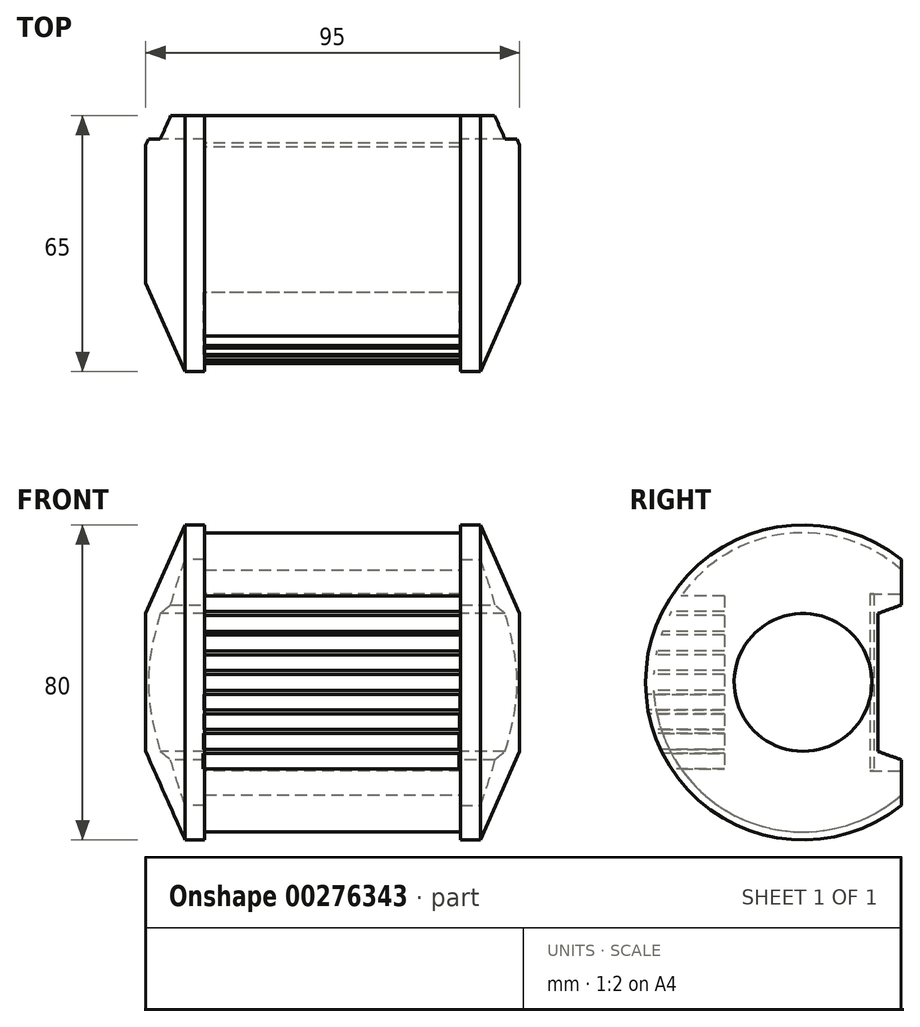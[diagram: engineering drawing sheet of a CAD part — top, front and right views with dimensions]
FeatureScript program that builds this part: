
annotation { "Feature Type Name" : "Feature", "Feature Type Description" : "" }
export const myFeature = defineFeature(function(context is Context, id is Id, definition is map)
    precondition{}
    {
        {
            var Q0;
            Q0=qCreatedBy(makeId("Right.planeOp"),FACE);
            var sketch = newSketch(context, id + "F0", { "sketchPlane" : qUnion([Q0])});
            skCircle(sketch, "E0", {"center": v(0, 0) * mm, "radius": 40 * mm});
            skSolve(sketch);
        }
        {
            var Q0;
            Q0=qCreatedBy(makeId("Right.planeOp"),FACE);
            cPlane(context, id + "F1", {"entities" : qUnion([Q0]), "cplaneType" : CPlaneType.OFFSET, "offset" : 10 * mm, "width" : 150 * mm, "height" : 150 * mm});
        }
        {
            var Q0;
            Q0=qCreatedBy(id+"F1.planeOp",FACE);
            var sketch = newSketch(context, id + "F2", { "sketchPlane" : qUnion([Q0])});
            skCircle(sketch, "E1", {"center": v(0, 0) * mm, "radius": 17.5 * mm});
            skSolve(sketch);
        }
        {
            var Q0;
            Q0=makeQuery(id+"F0.imprint","IMPRINT",FACE,{"disambiguationData":[TD([[makeQuery(id+"F0.imprint","IMPRINT",EDGE,{"derivedFrom":sQuery(id+"F0.wireOp",EDGE,"E0")}),1.0]])]});
            var Q1;
            Q1=makeQuery(id+"F2.imprint","IMPRINT",FACE,{"disambiguationData":[TD([[makeQuery(id+"F2.imprint","IMPRINT",EDGE,{"derivedFrom":sQuery(id+"F2.wireOp",EDGE,"E1")}),1.0]])]});
            loft(context, id + "F3", {"sheetProfilesArray" : [{ "sheetProfileEntities" : qUnion([Q0]) }, { "sheetProfileEntities" : qUnion([Q1]) }]});
        }
        {
            var Q0;
            Q0 = qSketchRegion(id + "F0", true);
            extrude(context, id + "F4", {"entities" : qUnion([Q0]), "operationType" : NewBodyOperationType.ADD, "oppositeDirection" : true, "depth" : 5 * mm});
        }
        {
            var Q0;
            Q0=qCreatedBy(id+"F1.planeOp",FACE);
            cPlane(context, id + "F5", {"entities" : qUnion([Q0]), "cplaneType" : CPlaneType.OFFSET, "offset" : 95 * mm, "oppositeDirection" : true, "width" : 150 * mm, "height" : 150 * mm});
        }
        {
            var Q0;
            Q0=qCreatedBy(id+"F1.planeOp",FACE);
            cPlane(context, id + "F6", {"entities" : qUnion([Q0]), "cplaneType" : CPlaneType.OFFSET, "offset" : 47.5 * mm, "oppositeDirection" : true, "width" : 150 * mm, "height" : 150 * mm});
        }
        {
            var Q0;
            Q0=qCreatedBy(id+"F5.planeOp",FACE);
            cPlane(context, id + "F7", {"entities" : qUnion([Q0]), "cplaneType" : CPlaneType.OFFSET, "offset" : 10 * mm, "width" : 150 * mm, "height" : 150 * mm});
        }
        {
            var Q0;
            Q0=qCreatedBy(id+"F7.planeOp",FACE);
            var sketch = newSketch(context, id + "F8", { "sketchPlane" : qUnion([Q0])});
            skCircle(sketch, "E2", {"center": v(0, 0) * mm, "radius": 40 * mm});
            skSolve(sketch);
        }
        {
            var Q0;
            Q0=qCreatedBy(id+"F5.planeOp",FACE);
            var sketch = newSketch(context, id + "F9", { "sketchPlane" : qUnion([Q0])});
            skCircle(sketch, "E3", {"center": v(0, 0) * mm, "radius": 17.5 * mm});
            skSolve(sketch);
        }
        {
            var Q0;
            Q0=makeQuery(id+"F8.imprint","IMPRINT",FACE,{"disambiguationData":[TD([[makeQuery(id+"F8.imprint","IMPRINT",EDGE,{"derivedFrom":sQuery(id+"F8.wireOp",EDGE,"E2")}),1.0]])]});
            var Q1;
            Q1=makeQuery(id+"F9.imprint","IMPRINT",FACE,{"disambiguationData":[TD([[makeQuery(id+"F9.imprint","IMPRINT",EDGE,{"derivedFrom":sQuery(id+"F9.wireOp",EDGE,"E3")}),1.0]])]});
            loft(context, id + "F10", {"sheetProfilesArray" : [{ "sheetProfileEntities" : qUnion([Q0]) }, { "sheetProfileEntities" : qUnion([Q1]) }]});
        }
        {
            var Q0;
            Q0=makeQuery(id+"F10.opLoft","CAP_FACE",FACE,{"disambiguationData":[OSD([makeQuery(id+"F8.imprint","IMPRINT",FACE,{"disambiguationData":[TD([[makeQuery(id+"F8.imprint","IMPRINT",EDGE,{"derivedFrom":sQuery(id+"F8.wireOp",EDGE,"E2")}),1.0]])]})])],"isStart":true});
            extrude(context, id + "F11", {"entities" : qUnion([Q0]), "operationType" : NewBodyOperationType.ADD, "depth" : 5 * mm});
        }
        {
            var Q0;
            Q0=makeQuery(id+"F4.opExtrude","CAP_FACE",FACE,{"disambiguationData":[OSD([sQuery(id+"F0.wireOp",EDGE,"E0")])],"isStart":false});
            var sketch = newSketch(context, id + "F12", { "sketchPlane" : qUnion([Q0])});
            skCircle(sketch, "E4", {"center": v(0, 0) * mm, "radius": 38 * mm});
            skSolve(sketch);
        }
        {
            var Q0;
            Q0 = qSketchRegion(id + "F12", true);
            extrude(context, id + "F13", {"entities" : qUnion([Q0]), "depth" : 65 * mm});
        }
        {
            var Q0;
            Q0=makeQuery(id+"F10.opLoft","CAP_FACE",FACE,{"disambiguationData":[OSD([makeQuery(id+"F9.imprint","IMPRINT",FACE,{"disambiguationData":[TD([[makeQuery(id+"F9.imprint","IMPRINT",EDGE,{"derivedFrom":sQuery(id+"F9.wireOp",EDGE,"E3")}),1.0]])]})])],"isStart":true});
            var sketch = newSketch(context, id + "F14", { "sketchPlane" : qUnion([Q0])});
            skLineSegment(sketch, "E5.bottom", {"start": v(-25, -139.46) * mm, "end": v(-147.73, -139.46) * mm});
            skLineSegment(sketch, "E5.top", {"start": v(-25, 136.68) * mm, "end": v(-147.73, 136.68) * mm});
            skLineSegment(sketch, "E5.left", {"start": v(-25, -139.46) * mm, "end": v(-25, 136.68) * mm});
            skLineSegment(sketch, "E5.right", {"start": v(-147.73, -139.46) * mm, "end": v(-147.73, 136.68) * mm});
            skSolve(sketch);
        }
        {
            var Q0;
            Q0=makeQuery(id+"F14.imprint","IMPRINT",FACE,{"disambiguationData":[TD([[makeQuery(id+"F14.imprint","IMPRINT",EDGE,{"derivedFrom":sQuery(id+"F14.wireOp",EDGE,"E5.bottom")}),-1.0]])]});
            extrude(context, id + "F15", {"entities" : qUnion([Q0]), "operationType" : NewBodyOperationType.REMOVE, "oppositeDirection" : true, "depth" : 100 * mm});
        }
        {
            var Q0;
            Q0=makeQuery(id+"F10.opLoft","CAP_FACE",FACE,{"disambiguationData":[OSD([makeQuery(id+"F9.imprint","IMPRINT",FACE,{"disambiguationData":[TD([[makeQuery(id+"F9.imprint","IMPRINT",EDGE,{"derivedFrom":sQuery(id+"F9.wireOp",EDGE,"E3")}),1.0]])]})])],"isStart":true});
            var sketch = newSketch(context, id + "F16", { "sketchPlane" : qUnion([Q0])});
            skLineSegment(sketch, "E6", {"start": v(-29.88, 21.46) * mm, "end": v(-19, 17.5) * mm});
            skLineSegment(sketch, "E7", {"start": v(-19, 17.5) * mm, "end": v(-19, -17.5) * mm});
            skLineSegment(sketch, "E8", {"start": v(-19, -17.5) * mm, "end": v(-29.88, -21.46) * mm});
            skLineSegment(sketch, "E9", {"start": v(-29.88, 21.46) * mm, "end": v(-29.88, -21.46) * mm});
            skSolve(sketch);
        }
        {
            var Q0;
            Q0=makeQuery(id+"F16.imprint","IMPRINT",FACE,{"disambiguationData":[TD([[makeQuery(id+"F16.imprint","IMPRINT",EDGE,{"derivedFrom":sQuery(id+"F16.wireOp",EDGE,"E6")}),-1.0]])]});
            extrude(context, id + "F17", {"entities" : qUnion([Q0]), "operationType" : NewBodyOperationType.REMOVE, "oppositeDirection" : true, "depth" : 100 * mm});
        }
        {
            var Q0;
            Q0=makeQuery(id+"F17.boolean.opBoolean","SPLIT",FACE,{"disambiguationData":[TD([makeQuery(id+"F17.opExtrude","SWEPT_FACE",FACE,{"disambiguationData":[OSD([sQuery(id+"F16.wireOp",EDGE,"E6")])]})])],"derivedFrom":makeQuery(id+"F15.boolean.opBoolean","COPY",FACE,{"derivedFrom":makeQuery(id+"F15.opExtrude","SWEPT_FACE",FACE,{"disambiguationData":[OSD([sQuery(id+"F14.wireOp",EDGE,"E5.left")])]})})});
            var sketch = newSketch(context, id + "F18", { "sketchPlane" : qUnion([Q0])});
            skLineSegment(sketch, "E10.bottom", {"start": v(5, 22.5) * mm, "end": v(70, 22.5) * mm});
            skLineSegment(sketch, "E10.top", {"start": v(5, -22.5) * mm, "end": v(70, -22.5) * mm});
            skLineSegment(sketch, "E10.left", {"start": v(5, 22.5) * mm, "end": v(5, -22.5) * mm});
            skLineSegment(sketch, "E10.right", {"start": v(70, 22.5) * mm, "end": v(70, -22.5) * mm});
            skSolve(sketch);
        }
        {
            var Q0;
            {var subQ0=sQuery(id+"F18.wireOp",EDGE,"E10.top");Q0=makeQuery(id+"F18.imprint","IMPRINT",FACE,{"disambiguationData":[TD([[makeQuery(id+"F18.imprint","IMPRINT",EDGE,{"derivedFrom":subQ0}),1.0]])]});}
            extrude(context, id + "F19", {"entities" : qUnion([Q0]), "operationType" : NewBodyOperationType.REMOVE, "oppositeDirection" : true, "depth" : 8 * mm});
        }
        {
            var Q0;
            Q0=makeQuery(id+"F19.boolean.opBoolean","COPY",FACE,{"derivedFrom":makeQuery(id+"F19.opExtrude","CAP_FACE",FACE,{"disambiguationData":[OSD([sQuery(id+"F14.wireOp",EDGE,"E5.left"),sQuery(id+"F16.wireOp",EDGE,"E6"),sQuery(id+"F18.wireOp",EDGE,"E10.top"),sQuery(id+"F18.wireOp",EDGE,"E10.left"),sQuery(id+"F18.wireOp",EDGE,"E10.right")])],"isStart":false})});
            extrude(context, id + "F20", {"entities" : qUnion([Q0]), "depth" : 1 * mm});
        }
        {
            var Q0;
            Q0=qCreatedBy(makeId("Front.planeOp"),FACE);
            cPlane(context, id + "F21", {"entities" : qUnion([Q0]), "cplaneType" : CPlaneType.OFFSET, "offset" : 40 * mm, "width" : 150 * mm, "height" : 150 * mm});
        }
        {
            var Q0;
            Q0=qCreatedBy(id+"F21.planeOp",FACE);
            var sketch = newSketch(context, id + "F22", { "sketchPlane" : qUnion([Q0])});
            skLineSegment(sketch, "E11.bottom", {"start": v(-5, 2) * mm, "end": v(-70, 2) * mm});
            skLineSegment(sketch, "E11.top", {"start": v(-5, -2) * mm, "end": v(-70, -2) * mm});
            skLineSegment(sketch, "E11.left", {"start": v(-5, 2) * mm, "end": v(-5, -2) * mm});
            skLineSegment(sketch, "E11.right", {"start": v(-70, 2) * mm, "end": v(-70, -2) * mm});
            skLineSegment(sketch, "E12.0.1.0", {"start": v(-5, 7) * mm, "end": v(-70, 7) * mm});
            skLineSegment(sketch, "E12.0.1.1", {"start": v(-5, 7) * mm, "end": v(-5, 3) * mm});
            skLineSegment(sketch, "E12.0.1.2", {"start": v(-5, 3) * mm, "end": v(-70, 3) * mm});
            skLineSegment(sketch, "E12.0.1.3", {"start": v(-70, 7) * mm, "end": v(-70, 3) * mm});
            skLineSegment(sketch, "E12.0.2.0", {"start": v(-5, 12) * mm, "end": v(-70, 12) * mm});
            skLineSegment(sketch, "E12.0.2.1", {"start": v(-5, 12) * mm, "end": v(-5, 8) * mm});
            skLineSegment(sketch, "E12.0.2.2", {"start": v(-5, 8) * mm, "end": v(-70, 8) * mm});
            skLineSegment(sketch, "E12.0.2.3", {"start": v(-70, 12) * mm, "end": v(-70, 8) * mm});
            skLineSegment(sketch, "E12.direction1", {"start": v(-70, -2) * mm, "end": v(-45, -2) * mm, "construction": true});
            skLineSegment(sketch, "E12.direction2", {"start": v(-70, -2) * mm, "end": v(-70, 3) * mm, "construction": true});
            skLineSegment(sketch, "E13.0.0.3", {"start": v(-5, 17) * mm, "end": v(-70, 17) * mm});
            skLineSegment(sketch, "E13.3.0.3", {"start": v(-5, 17) * mm, "end": v(-5, 13) * mm});
            skLineSegment(sketch, "E13.6.0.3", {"start": v(-5, 13) * mm, "end": v(-70, 13) * mm});
            skLineSegment(sketch, "E13.9.0.3", {"start": v(-70, 17) * mm, "end": v(-70, 13) * mm});
            skLineSegment(sketch, "E13.0.0.4", {"start": v(-5, 22) * mm, "end": v(-70, 22) * mm});
            skLineSegment(sketch, "E13.3.0.4", {"start": v(-5, 22) * mm, "end": v(-5, 18) * mm});
            skLineSegment(sketch, "E13.6.0.4", {"start": v(-5, 18) * mm, "end": v(-70, 18) * mm});
            skLineSegment(sketch, "E13.9.0.4", {"start": v(-70, 22) * mm, "end": v(-70, 18) * mm});
            skLineSegment(sketch, "E14.0.1.1", {"start": v(-5.12, -7) * mm, "end": v(-70.12, -7) * mm});
            skLineSegment(sketch, "E14.0.1.2", {"start": v(-5.12, -3) * mm, "end": v(-70.12, -3) * mm});
            skLineSegment(sketch, "E14.0.1.3", {"start": v(-5.12, -3) * mm, "end": v(-5.12, -7) * mm});
            skLineSegment(sketch, "E14.0.2.1", {"start": v(-5.23, -12) * mm, "end": v(-70.23, -12) * mm});
            skLineSegment(sketch, "E14.0.2.2", {"start": v(-5.23, -8) * mm, "end": v(-70.23, -8) * mm});
            skLineSegment(sketch, "E14.0.2.3", {"start": v(-5.23, -8) * mm, "end": v(-5.23, -12) * mm});
            skLineSegment(sketch, "E14.0.3.1", {"start": v(-5.35, -17) * mm, "end": v(-70.35, -17) * mm});
            skLineSegment(sketch, "E14.0.3.2", {"start": v(-5.35, -13) * mm, "end": v(-70.35, -13) * mm});
            skLineSegment(sketch, "E14.0.3.3", {"start": v(-5.35, -13) * mm, "end": v(-5.35, -17) * mm});
            skLineSegment(sketch, "E14.0.4.1", {"start": v(-5.46, -22) * mm, "end": v(-70.46, -22) * mm});
            skLineSegment(sketch, "E14.0.4.2", {"start": v(-5.46, -18) * mm, "end": v(-70.46, -18) * mm});
            skLineSegment(sketch, "E14.0.4.3", {"start": v(-5.46, -18) * mm, "end": v(-5.46, -22) * mm});
            skLineSegment(sketch, "E15", {"start": v(-70.12, -3) * mm, "end": v(-70.12, -7) * mm});
            skLineSegment(sketch, "E16", {"start": v(-70.23, -8) * mm, "end": v(-70.23, -12) * mm});
            skLineSegment(sketch, "E17", {"start": v(-70.35, -13) * mm, "end": v(-70.35, -17) * mm});
            skLineSegment(sketch, "E18", {"start": v(-70.46, -18) * mm, "end": v(-70.46, -22) * mm});
            skSolve(sketch);
        }
        {
            var Q0;
            Q0 = qSketchRegion(id + "F22", true);
            extrude(context, id + "F23", {"entities" : qUnion([Q0]), "operationType" : NewBodyOperationType.REMOVE, "oppositeDirection" : true, "depth" : 20 * mm});
        }
    });
